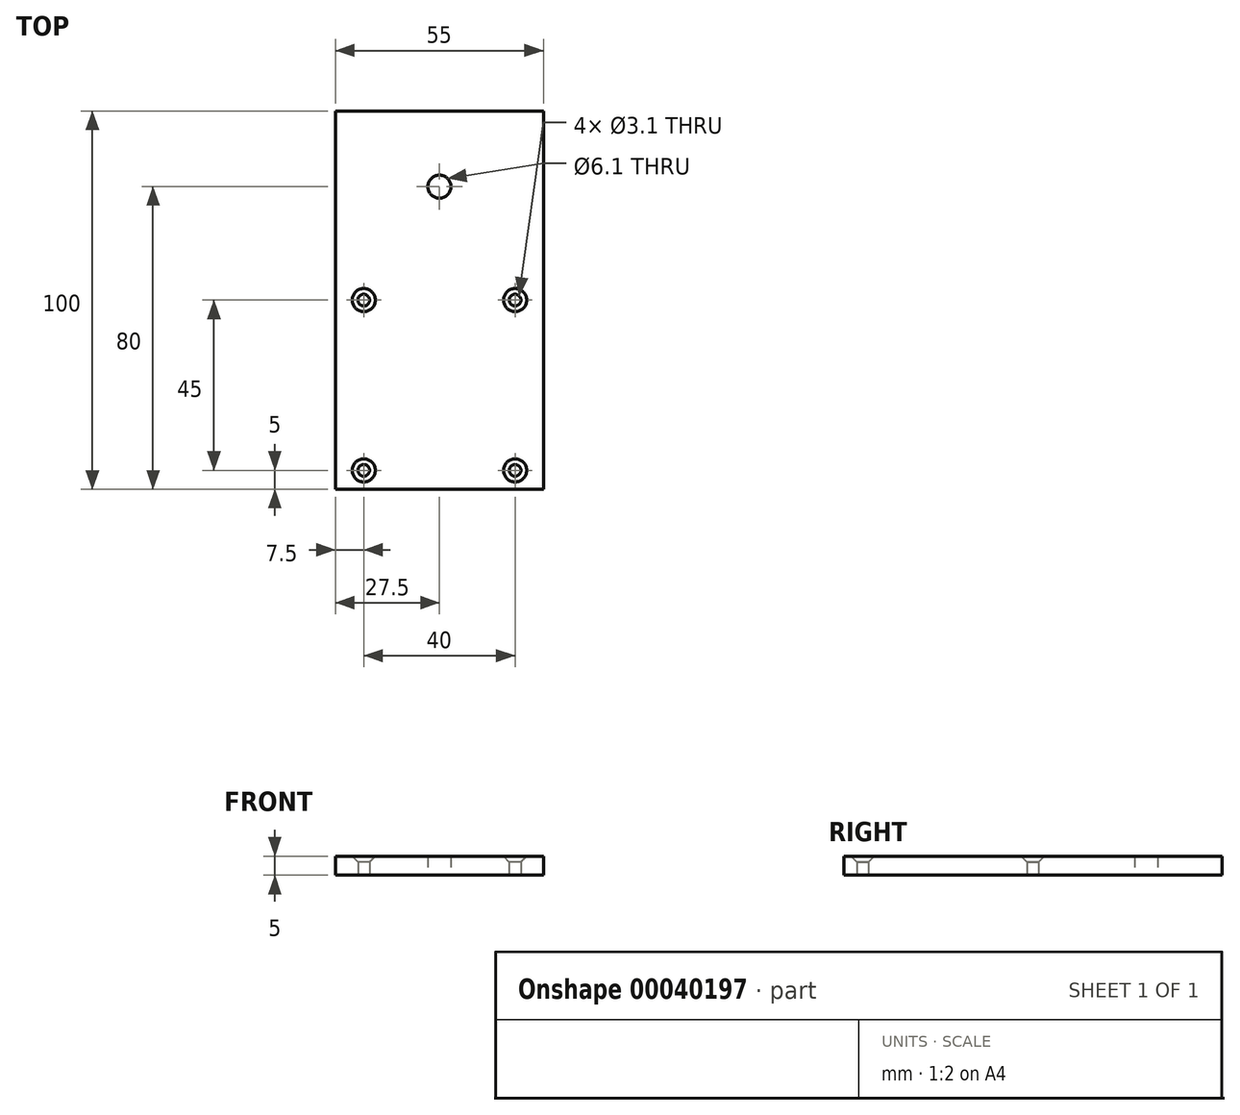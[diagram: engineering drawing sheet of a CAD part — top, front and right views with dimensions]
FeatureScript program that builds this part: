
annotation { "Feature Type Name" : "Feature", "Feature Type Description" : "" }
export const myFeature = defineFeature(function(context is Context, id is Id, definition is map)
    precondition{}
    {
        {
            var Q0;
            Q0=qCreatedBy(makeId("Top.planeOp"),FACE);
            var sketch = newSketch(context, id + "F0", { "sketchPlane" : qUnion([Q0])});
            skLineSegment(sketch, "E0.rect.bottom", {"start": v(27.5, -27.5) * mm, "end": v(-27.5, -27.5) * mm});
            skLineSegment(sketch, "E0.rect.top", {"start": v(27.5, 72.5) * mm, "end": v(-27.5, 72.5) * mm});
            skLineSegment(sketch, "E0.rect.left", {"start": v(27.5, -27.5) * mm, "end": v(27.5, 72.5) * mm});
            skLineSegment(sketch, "E0.rect.right", {"start": v(-27.5, -27.5) * mm, "end": v(-27.5, 72.5) * mm});
            skPoint(sketch, "E0.rect.middle", {"position": v(0, 0) * mm});
            skLineSegment(sketch, "E1.rect.bottom", {"start": v(20, -22.5) * mm, "end": v(-20, -22.5) * mm, "construction": true});
            skLineSegment(sketch, "E1.rect.top", {"start": v(20, 22.5) * mm, "end": v(-20, 22.5) * mm, "construction": true});
            skLineSegment(sketch, "E1.rect.left", {"start": v(20, -22.5) * mm, "end": v(20, 22.5) * mm, "construction": true});
            skLineSegment(sketch, "E1.rect.right", {"start": v(-20, -22.5) * mm, "end": v(-20, 22.5) * mm, "construction": true});
            skCircle(sketch, "E2", {"center": v(0, 52.5) * mm, "radius": 3.05 * mm});
            skCircle(sketch, "E3", {"center": v(-20, 22.5) * mm, "radius": 1.55 * mm});
            skCircle(sketch, "E4", {"center": v(20, 22.5) * mm, "radius": 1.55 * mm});
            skCircle(sketch, "E5", {"center": v(20, -22.5) * mm, "radius": 1.55 * mm});
            skCircle(sketch, "E6", {"center": v(-20, -22.5) * mm, "radius": 1.55 * mm});
            skSolve(sketch);
        }
        {
            var Q0;
            Q0=makeQuery(id+"F0.imprint","IMPRINT",FACE,{"disambiguationData":[TD([[makeQuery(id+"F0.imprint","IMPRINT",EDGE,{"derivedFrom":sQuery(id+"F0.wireOp",EDGE,"E0.rect.bottom")}),-1.0]])]});
            extrude(context, id + "F1", {"entities" : qUnion([Q0]), "depth" : 5 * mm});
        }
        {
            var Q0;
            Q0=makeQuery(id+"F1.opExtrude","CAP_EDGE",EDGE,{"disambiguationData":[OSD([sQuery(id+"F0.wireOp",EDGE,"E3")])],"isStart":false});
            var Q1;
            Q1=makeQuery(id+"F1.opExtrude","CAP_EDGE",EDGE,{"disambiguationData":[OSD([sQuery(id+"F0.wireOp",EDGE,"E4")])],"isStart":false});
            var Q2;
            Q2=makeQuery(id+"F1.opExtrude","CAP_EDGE",EDGE,{"disambiguationData":[OSD([sQuery(id+"F0.wireOp",EDGE,"E5")])],"isStart":false});
            var Q3;
            Q3=makeQuery(id+"F1.opExtrude","CAP_EDGE",EDGE,{"disambiguationData":[OSD([sQuery(id+"F0.wireOp",EDGE,"E6")])],"isStart":false});
            chamfer(context, id + "F2", {"entities" : qUnion([Q0, Q1, Q2, Q3]), "width" : 1.5 * mm, "tangentPropagation" : true});
        }
    });
